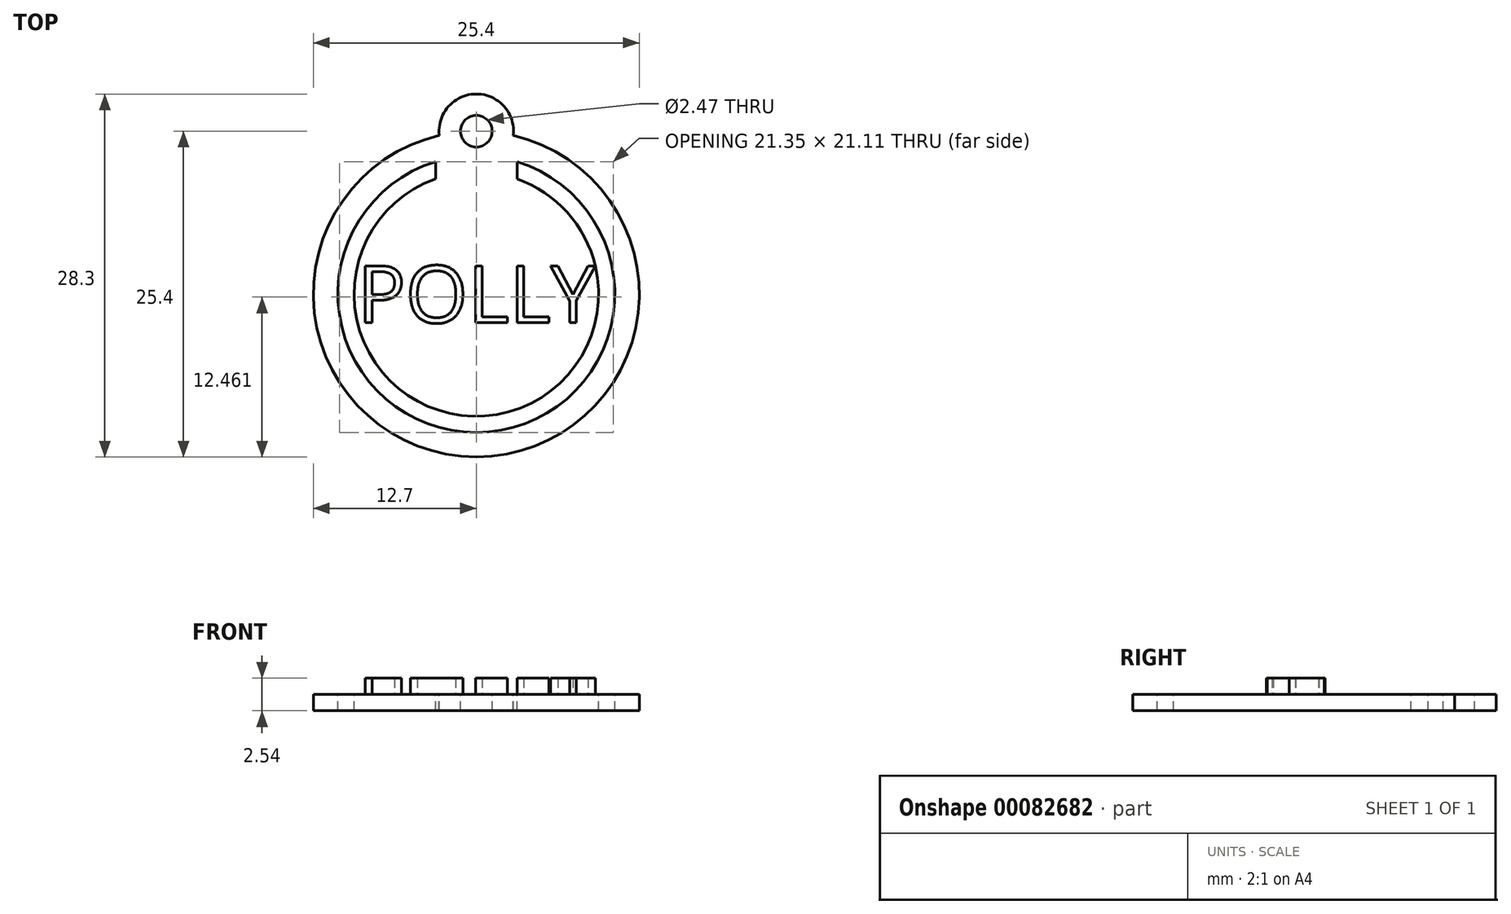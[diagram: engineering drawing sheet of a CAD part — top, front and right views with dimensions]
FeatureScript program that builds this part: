
annotation { "Feature Type Name" : "Feature", "Feature Type Description" : "" }
export const myFeature = defineFeature(function(context is Context, id is Id, definition is map)
    precondition{}
    {
        {
            var Q0;
            Q0=qCreatedBy(makeId("Top.planeOp"),FACE);
            var sketch = newSketch(context, id + "F0", { "sketchPlane" : qUnion([Q0])});
            skCircle(sketch, "E0", {"center": v(0, 0) * mm, "radius": 12.7 * mm});
            skSolve(sketch);
        }
        {
            var Q0;
            Q0=makeQuery(id+"F0.imprint","IMPRINT",FACE,{"disambiguationData":[TD([[makeQuery(id+"F0.imprint","IMPRINT",EDGE,{"derivedFrom":sQuery(id+"F0.wireOp",EDGE,"E0")}),1.0]])]});
            extrude(context, id + "F1", {"entities" : qUnion([Q0]), "depth" : 1.27 * mm});
        }
        {
            var Q0;
            Q0=makeQuery(id+"F1.opExtrude","CAP_FACE",FACE,{"disambiguationData":[OSD([sQuery(id+"F0.wireOp",EDGE,"E0")])],"isStart":false});
            var sketch = newSketch(context, id + "F2", { "sketchPlane" : qUnion([Q0])});
            skArc(sketch, "E1", {"start": v(-3.18, 10.32) * mm, "mid": v(0, -10.8) * mm, "end": v(3.18, 10.32) * mm});
            skArc(sketch, "E2", {"start": v(-3.18, 8.98) * mm, "mid": v(0, -9.53) * mm, "end": v(3.17, 8.98) * mm});
            skLineSegment(sketch, "E3", {"start": v(-3.18, 10.32) * mm, "end": v(-3.18, 8.98) * mm});
            skLineSegment(sketch, "E4", {"start": v(3.18, 10.32) * mm, "end": v(3.18, 8.98) * mm});
            skPoint(sketch, "E5.orphan", {"position": v(-3.18, 13.9) * mm});
            skPoint(sketch, "E6.orphan", {"position": v(3.18, 13.9) * mm});
            skPoint(sketch, "E7.orphan", {"position": v(-3.18, 0) * mm});
            skPoint(sketch, "E8.orphan", {"position": v(3.18, 0) * mm});
            skSolve(sketch);
        }
        {
            var Q0;
            Q0=qCreatedBy(makeId("Front.planeOp"),FACE);
            var sketch = newSketch(context, id + "F3", { "sketchPlane" : qUnion([Q0])});
            skSolve(sketch);
        }
        {
            var Q0;
            Q0 = qSketchRegion(id + "F3", true);
            var Q1;
            Q1=makeQuery(id+"F2.imprint","IMPRINT",FACE,{"disambiguationData":[TD([[makeQuery(id+"F2.imprint","IMPRINT",EDGE,{"derivedFrom":sQuery(id+"F2.wireOp",EDGE,"E1")}),1.0]])]});
            extrude(context, id + "F4", {"entities" : qUnion([Q0, Q1]), "operationType" : NewBodyOperationType.REMOVE, "oppositeDirection" : true, "depth" : 6.23 * mm});
        }
        {
            var Q0;
            Q0=makeQuery(id+"F1.opExtrude","CAP_FACE",FACE,{"disambiguationData":[OSD([sQuery(id+"F0.wireOp",EDGE,"E0")])],"isStart":false});
            var sketch = newSketch(context, id + "F5", { "sketchPlane" : qUnion([Q0])});
            skText(sketch, "E9", { "text": "POLLY", "fontName": "OpenSans-Regular.ttf"});
            const initialGuessF5  = {"E9": [-0.00926, -0.00224, 1, 0, 0.00448]};
            skSetInitialGuess(sketch, initialGuessF5);
            skSolve(sketch);
        }
        {
            var Q0;
            Q0 = qSketchRegion(id + "F5", true);
            extrude(context, id + "F6", {"entities" : qUnion([Q0]), "operationType" : NewBodyOperationType.ADD, "depth" : 1.27 * mm});
        }
        {
            var Q0;
            {var subQ0=sQuery(id+"F0.wireOp",EDGE,"E0");Q0=makeQuery(id+"F6.boolean.opBoolean","SPLIT",FACE,{"disambiguationData":[TD([makeQuery(id+"F1.opExtrude","SWEPT_FACE",FACE,{"disambiguationData":[OSD([subQ0])]})])],"derivedFrom":makeQuery(id+"F1.opExtrude","CAP_FACE",FACE,{"disambiguationData":[OSD([subQ0])],"isStart":false})});}
            var sketch = newSketch(context, id + "F7", { "sketchPlane" : qUnion([Q0])});
            skPoint(sketch, "E10.center.orphan", {"position": v(0, 12.7) * mm});
            skArc(sketch, "E11", {"start": v(2.88, 12.36) * mm, "mid": v(-0.01, 15.6) * mm, "end": v(-2.88, 12.33) * mm});
            skSolve(sketch);
        }
        {
            var Q0;
            {var subQ0=sQuery(id+"F7.wireOp",EDGE,"E11");var subQ1=makeQuery(id+"F1.opExtrude","CAP_EDGE",EDGE,{"disambiguationData":[OSD([sQuery(id+"F0.wireOp",EDGE,"E0")])],"isStart":false});var subQ2=makeQuery(id+"F7.imprint","INTERSECT",VERTEX,{"disambiguationData":[OD(0.0)],"derivedFrom":[subQ1,subQ0]});Q0=makeQuery(id+"F7.imprint","IMPRINT",FACE,{"disambiguationData":[TD([[makeQuery(id+"F7.imprint","IMPRINT",EDGE,{"disambiguationData":[TD([[subQ2,1.0]])],"derivedFrom":subQ0}),1.0]])]});}
            extrude(context, id + "F8", {"entities" : qUnion([Q0]), "operationType" : NewBodyOperationType.ADD, "oppositeDirection" : true, "depth" : 1.27 * mm});
        }
        {
            var Q0;
            {var subQ0=sQuery(id+"F0.wireOp",EDGE,"E0");Q0=makeQuery(id+"F8.boolean.opBoolean","MERGE",FACE,{"derivedFrom":[makeQuery(id+"F6.boolean.opBoolean","SPLIT",FACE,{"disambiguationData":[TD([makeQuery(id+"F1.opExtrude","SWEPT_FACE",FACE,{"disambiguationData":[OSD([subQ0])]})])],"derivedFrom":makeQuery(id+"F1.opExtrude","CAP_FACE",FACE,{"disambiguationData":[OSD([subQ0])],"isStart":false})}),makeQuery(id+"F8.opExtrude","CAP_FACE",FACE,{"disambiguationData":[OSD([subQ0,sQuery(id+"F7.wireOp",EDGE,"E11")])],"isStart":true})]});}
            var sketch = newSketch(context, id + "F9", { "sketchPlane" : qUnion([Q0])});
            skCircle(sketch, "E12", {"center": v(0, 12.7) * mm, "radius": 1.23 * mm});
            skSolve(sketch);
        }
        {
            var Q0;
            Q0=makeQuery(id+"F9.imprint","IMPRINT",FACE,{"disambiguationData":[TD([[makeQuery(id+"F9.imprint","IMPRINT",EDGE,{"derivedFrom":sQuery(id+"F9.wireOp",EDGE,"E12")}),1.0]])]});
            var Q1;
            Q1=sQuery(id+"F9.wireOp",EDGE,"E12");
            extrude(context, id + "F10", {"entities" : qUnion([Q0]), "operationType" : NewBodyOperationType.REMOVE, "surfaceEntities" : qUnion([Q1]), "endBound" : BoundingType.THROUGH_ALL, "oppositeDirection" : true, "depth" : 25.4 * mm});
        }
    });
